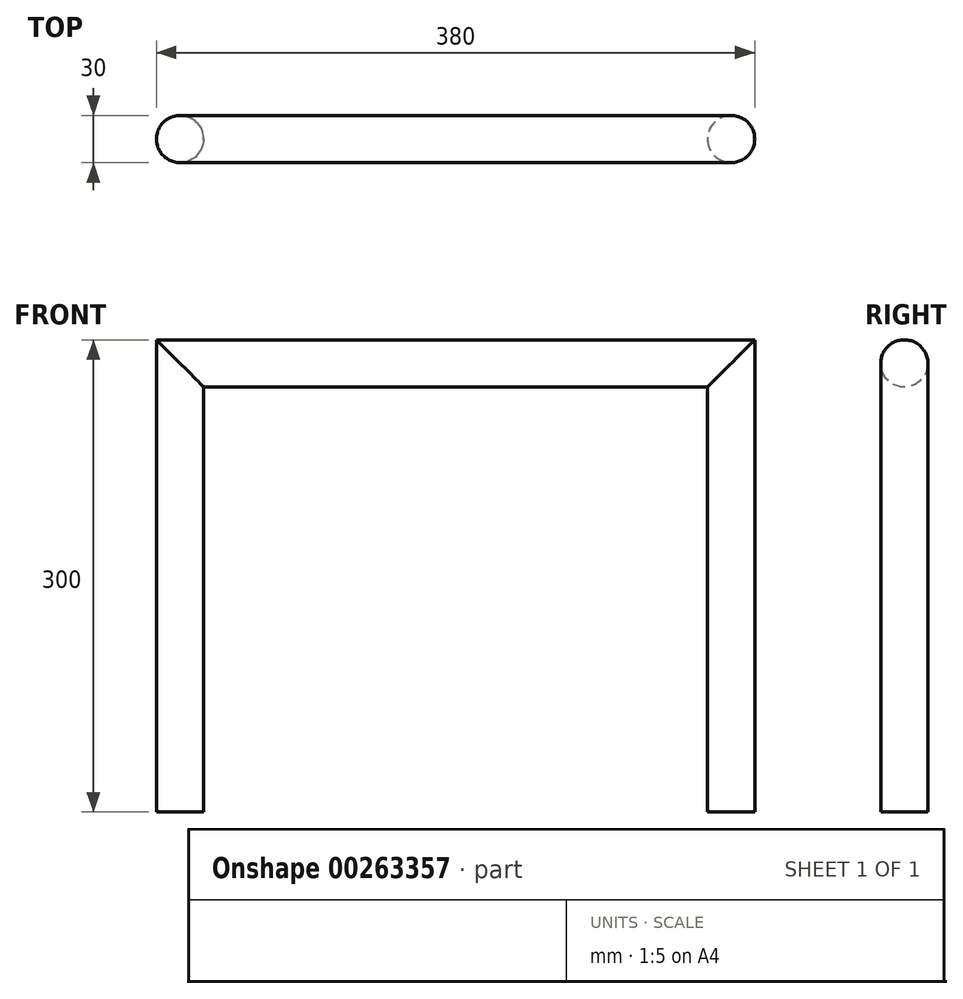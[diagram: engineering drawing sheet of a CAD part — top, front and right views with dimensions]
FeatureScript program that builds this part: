
annotation { "Feature Type Name" : "Feature", "Feature Type Description" : "" }
export const myFeature = defineFeature(function(context is Context, id is Id, definition is map)
    precondition{}
    {
        {
            var Q0;
            Q0=qCreatedBy(makeId("Top.planeOp"),FACE);
            var sketch = newSketch(context, id + "F0", { "sketchPlane" : qUnion([Q0])});
            skCircle(sketch, "E0", {"center": v(-175, 0) * mm, "radius": 15 * mm});
            skLineSegment(sketch, "E1", {"start": v(0, 0) * mm, "end": v(0, 112.69) * mm, "construction": true});
            skCircle(sketch, "E2.MirrorC", {"center": v(175, 0) * mm, "radius": 15 * mm});
            skSolve(sketch);
        }
        {
            var Q0;
            Q0 = qSketchRegion(id + "F0", true);
            extrude(context, id + "F1", {"entities" : qUnion([Q0]), "depth" : 300 * mm});
        }
        {
            var Q0;
            Q0=qCreatedBy(makeId("Front.planeOp"),FACE);
            var sketch = newSketch(context, id + "F2", { "sketchPlane" : qUnion([Q0])});
            skLineSegment(sketch, "E3", {"start": v(190, 300) * mm, "end": v(158.72, 268.72) * mm});
            skLineSegment(sketch, "E4", {"start": v(160, 0) * mm, "end": v(160, 300) * mm, "construction": true});
            skLineSegment(sketch, "E5", {"start": v(190, 300) * mm, "end": v(190, 0) * mm, "construction": true});
            skLineSegment(sketch, "E6", {"start": v(0, 0) * mm, "end": v(0, 294.23) * mm, "construction": true});
            skLineSegment(sketch, "E7.MirrorCS", {"start": v(-190, 300) * mm, "end": v(-158.72, 268.72) * mm});
            skLineSegment(sketch, "E8", {"start": v(158.72, 268.72) * mm, "end": v(-158.72, 268.72) * mm});
            skLineSegment(sketch, "E9", {"start": v(-190, 300) * mm, "end": v(190, 300) * mm});
            skSolve(sketch);
        }
        {
            var Q0;
            Q0=makeQuery(id+"F2.imprint","IMPRINT",FACE,{"disambiguationData":[TD([[makeQuery(id+"F2.imprint","IMPRINT",EDGE,{"derivedFrom":sQuery(id+"F2.wireOp",EDGE,"E3")}),-1.0]])]});
            extrude(context, id + "F3", {"entities" : qUnion([Q0]), "operationType" : NewBodyOperationType.REMOVE, "endBound" : BoundingType.THROUGH_ALL, "oppositeDirection" : true, "depth" : 25 * mm, "hasSecondDirection" : true, "secondDirectionBound" : SecondDirectionBoundingType.THROUGH_ALL, "secondDirectionOppositeDirection" : false, "secondDirectionDepth" : 25 * mm});
        }
        {
            var Q0;
            Q0=qCreatedBy(makeId("Right.planeOp"),FACE);
            var sketch = newSketch(context, id + "F4", { "sketchPlane" : qUnion([Q0])});
            skCircle(sketch, "E10.0.0", {"center": v(0, 285) * mm, "radius": 15 * mm});
            skSolve(sketch);
        }
        {
            var Q0;
            Q0 = qSketchRegion(id + "F4", true);
            var Q1;
            Q1=makeQuery(id+"F3.boolean.opBoolean","COPY",FACE,{"derivedFrom":makeQuery(id+"F3.opExtrude","SWEPT_FACE",FACE,{"disambiguationData":[OSD([sQuery(id+"F2.wireOp",EDGE,"E3")])]})});
            var Q2;
            Q2=makeQuery(id+"F3.boolean.opBoolean","COPY",FACE,{"derivedFrom":makeQuery(id+"F3.opExtrude","SWEPT_FACE",FACE,{"disambiguationData":[OSD([sQuery(id+"F2.wireOp",EDGE,"E7.MirrorCS")])]})});
            extrude(context, id + "F5", {"entities" : qUnion([Q0]), "operationType" : NewBodyOperationType.ADD, "endBound" : BoundingType.UP_TO_SURFACE, "endBoundEntityFace" : qUnion([Q1]), "depth" : 25 * mm, "hasSecondDirection" : true, "secondDirectionBound" : SecondDirectionBoundingType.UP_TO_SURFACE, "secondDirectionOppositeDirection" : true, "secondDirectionBoundEntityFace" : qUnion([Q2]), "secondDirectionDepth" : 25 * mm});
        }
    });
